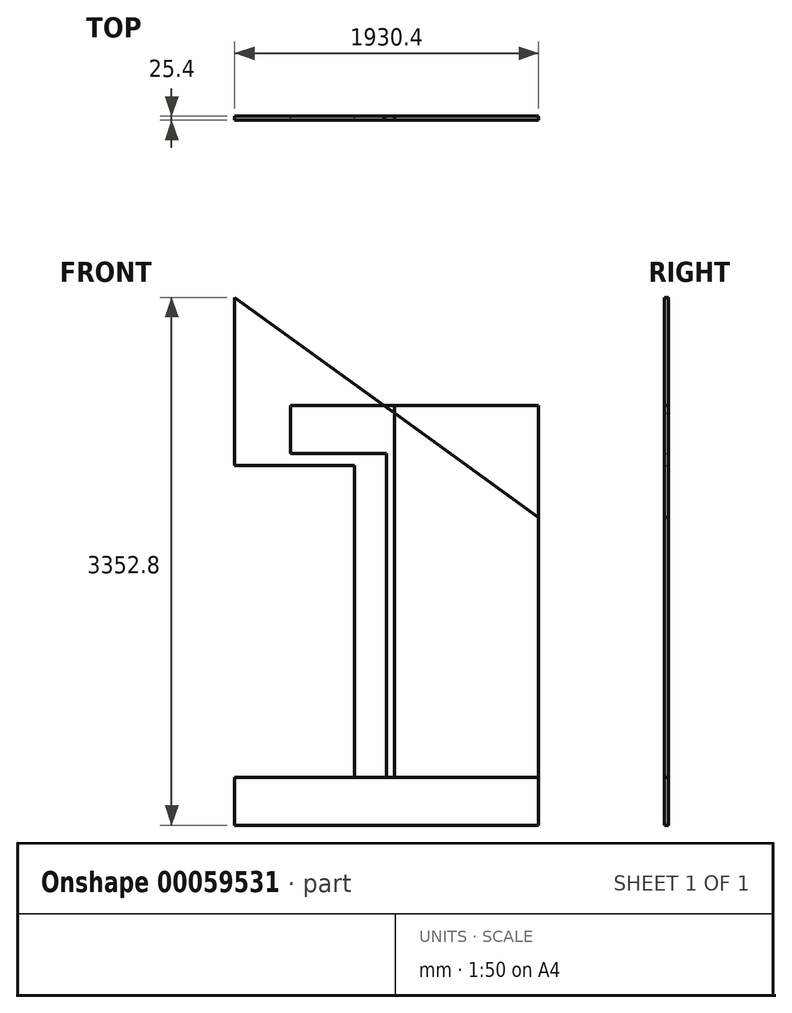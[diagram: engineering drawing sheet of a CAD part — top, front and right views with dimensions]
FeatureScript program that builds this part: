
annotation { "Feature Type Name" : "Feature", "Feature Type Description" : "" }
export const myFeature = defineFeature(function(context is Context, id is Id, definition is map)
    precondition{}
    {
        {
            var Q0;
            Q0=qCreatedBy(makeId("Front.planeOp"),FACE);
            var sketch = newSketch(context, id + "F0", { "sketchPlane" : qUnion([Q0])});
            skLineSegment(sketch, "E0", {"start": v(-914.4, 0) * mm, "end": v(-914.4, 2362.2) * mm});
            skLineSegment(sketch, "E1", {"start": v(0, 2362.2) * mm, "end": v(0, 0) * mm});
            skLineSegment(sketch, "E2", {"start": v(-965.2, 0) * mm, "end": v(-965.2, 2057.4) * mm});
            skLineSegment(sketch, "E3", {"start": v(-965.2, 2057.4) * mm, "end": v(-1574.8, 2057.4) * mm});
            skLineSegment(sketch, "E4", {"start": v(-1574.8, 2057.4) * mm, "end": v(-1574.8, 2362.2) * mm});
            skLineSegment(sketch, "E5", {"start": v(-1574.8, 2362.2) * mm, "end": v(0, 2362.2) * mm});
            skLineSegment(sketch, "E6", {"start": v(-1168.4, 0) * mm, "end": v(0, 0) * mm});
            skLineSegment(sketch, "E7", {"start": v(-1168.4, 0) * mm, "end": v(-1168.4, 1981.2) * mm});
            skLineSegment(sketch, "E8", {"start": v(-1168.4, 1981.2) * mm, "end": v(-1930.4, 1981.2) * mm});
            skLineSegment(sketch, "E9", {"start": v(-1930.4, 1981.2) * mm, "end": v(-1930.4, 3048) * mm});
            skLineSegment(sketch, "E10", {"start": v(-1930.4, 3048) * mm, "end": v(0, 1651) * mm});
            skLineSegment(sketch, "E11.bottom", {"start": v(0, 0) * mm, "end": v(-1930.4, 0) * mm});
            skLineSegment(sketch, "E11.top", {"start": v(0, -304.8) * mm, "end": v(-1930.4, -304.8) * mm});
            skLineSegment(sketch, "E11.left", {"start": v(0, 0) * mm, "end": v(0, -304.8) * mm});
            skLineSegment(sketch, "E11.right", {"start": v(-1930.4, 0) * mm, "end": v(-1930.4, -304.8) * mm});
            skSolve(sketch);
        }
        {
            var Q0;
            {var subQ4=sQuery(id+"F0.wireOp",EDGE,"E2");Q0=makeQuery(id+"F0.imprint","IMPRINT",FACE,{"disambiguationData":[TD([[makeQuery(id+"F0.imprint","IMPRINT",EDGE,{"derivedFrom":subQ4}),-1.0]])]});}
            var Q1;
            {var subQ0=sQuery(id+"F0.wireOp",EDGE,"E5");var subQ1=sQuery(id+"F0.wireOp",EDGE,"E0");var subQ2=makeQuery(id+"F0.imprint","INTERSECT",VERTEX,{"derivedFrom":[subQ1,subQ0]});Q1=makeQuery(id+"F0.imprint","IMPRINT",FACE,{"disambiguationData":[TD([[makeQuery(id+"F0.imprint","IMPRINT",EDGE,{"disambiguationData":[TD([[subQ2,1.0]])],"derivedFrom":subQ1}),-1.0]])]});}
            extrude(context, id + "F1", {"entities" : qUnion([Q0, Q1]), "depth" : 25.4 * mm});
        }
        {
            var Q0;
            {var subQ5=sQuery(id+"F0.wireOp",EDGE,"E2");Q0=makeQuery(id+"F0.imprint","IMPRINT",FACE,{"disambiguationData":[TD([[makeQuery(id+"F0.imprint","IMPRINT",EDGE,{"derivedFrom":subQ5}),1.0]])]});}
            var Q1;
            {var subQ0=sQuery(id+"F0.wireOp",EDGE,"E5");var subQ1=sQuery(id+"F0.wireOp",EDGE,"E0");var subQ2=makeQuery(id+"F0.imprint","INTERSECT",VERTEX,{"derivedFrom":[subQ1,subQ0]});Q1=makeQuery(id+"F0.imprint","IMPRINT",FACE,{"disambiguationData":[TD([[makeQuery(id+"F0.imprint","IMPRINT",EDGE,{"disambiguationData":[TD([[subQ2,1.0]])],"derivedFrom":subQ1}),1.0]])]});}
            var Q2;
            {var subQ0=sQuery(id+"F0.wireOp",EDGE,"E11.bottom");var subQ1=sQuery(id+"F0.wireOp",EDGE,"E0");var subQ2=makeQuery(id+"F0.imprint","INTERSECT",VERTEX,{"derivedFrom":[subQ1,subQ0]});Q2=makeQuery(id+"F0.imprint","IMPRINT",FACE,{"disambiguationData":[TD([[makeQuery(id+"F0.imprint","IMPRINT",EDGE,{"disambiguationData":[TD([[subQ2,-1.0]])],"derivedFrom":subQ1}),-1.0]])]});}
            extrude(context, id + "F2", {"entities" : qUnion([Q0, Q1, Q2]), "depth" : 25.4 * mm});
        }
        {
            var Q0;
            Q0=makeQuery(id+"F0.imprint","IMPRINT",FACE,{"disambiguationData":[TD([[makeQuery(id+"F0.imprint","IMPRINT",EDGE,{"derivedFrom":sQuery(id+"F0.wireOp",EDGE,"E11.top")}),-1.0]])]});
            extrude(context, id + "F3", {"entities" : qUnion([Q0]), "depth" : 25.4 * mm});
        }
    });
